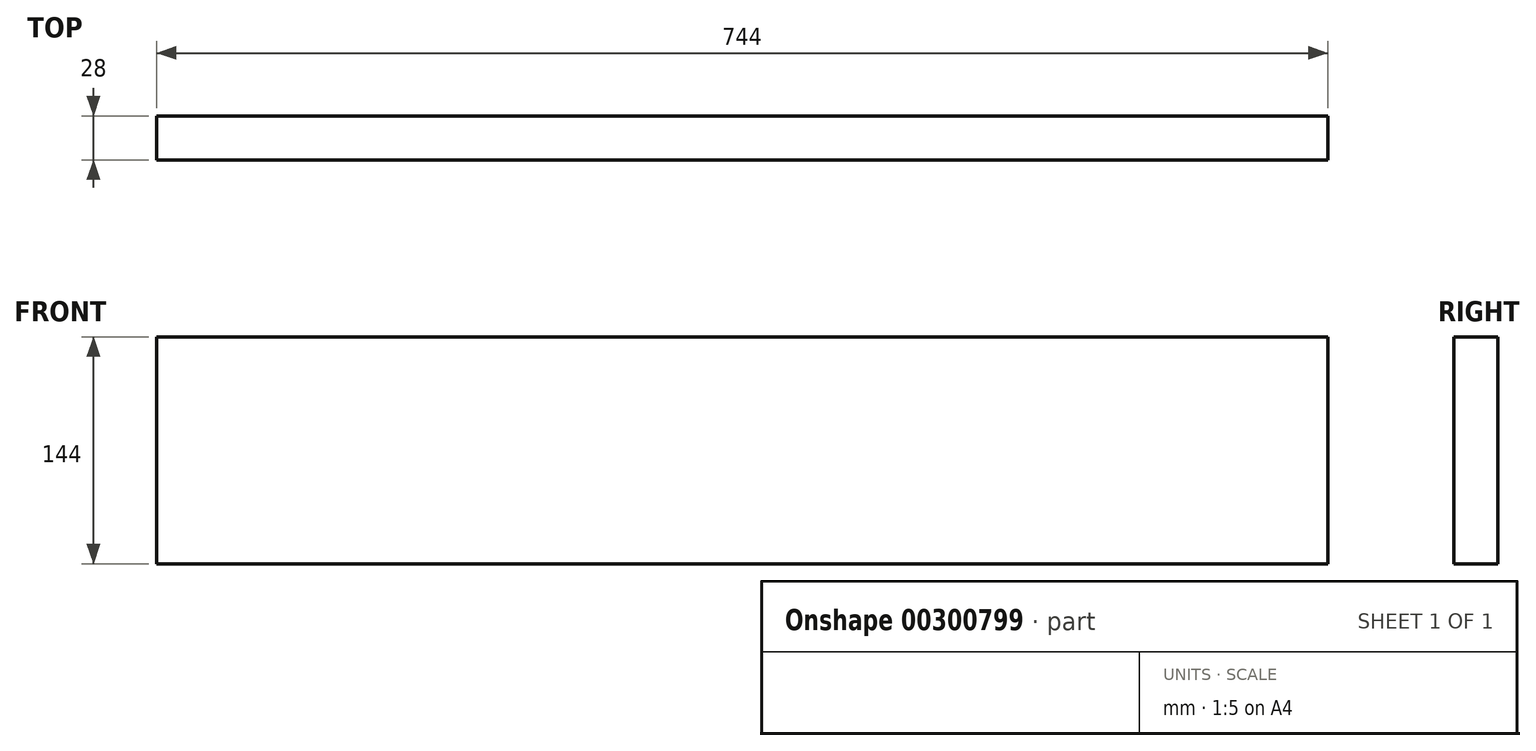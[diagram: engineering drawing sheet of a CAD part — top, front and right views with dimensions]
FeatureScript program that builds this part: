
annotation { "Feature Type Name" : "Feature", "Feature Type Description" : "" }
export const myFeature = defineFeature(function(context is Context, id is Id, definition is map)
    precondition{}
    {
        {
            var Q0;
            Q0=qCreatedBy(makeId("Front.planeOp"),FACE);
            var sketch = newSketch(context, id + "F0", { "sketchPlane" : qUnion([Q0])});
            skLineSegment(sketch, "E0.bottom", {"start": v(-918.71, -213.6) * mm, "end": v(941.29, -213.6) * mm});
            skLineSegment(sketch, "E0.top", {"start": v(-918.71, -573.6) * mm, "end": v(941.29, -573.6) * mm});
            skLineSegment(sketch, "E0.left", {"start": v(-918.71, -213.6) * mm, "end": v(-918.71, -573.6) * mm});
            skLineSegment(sketch, "E0.right", {"start": v(941.29, -213.6) * mm, "end": v(941.29, -573.6) * mm});
            skSolve(sketch);
        }
        {
            var Q0;
            Q0=makeQuery(id+"F0.imprint","IMPRINT",FACE,{"disambiguationData":[TD([[makeQuery(id+"F0.imprint","IMPRINT",EDGE,{"derivedFrom":sQuery(id+"F0.wireOp",EDGE,"E0.bottom")}),-1.0]])]});
            extrude(context, id + "F1", {"entities" : qUnion([Q0]), "depth" : 70 * mm});
        }
        {
            var Q0;
            Q0=makeQuery(id+"F1.opExtrude","SWEPT_BODY",BODY,{"disambiguationData":[OSD([sQuery(id+"F0.wireOp",EDGE,"E0.bottom"),sQuery(id+"F0.wireOp",EDGE,"E0.top"),sQuery(id+"F0.wireOp",EDGE,"E0.left"),sQuery(id+"F0.wireOp",EDGE,"E0.right")])]});
            var Q1;
            Q1=makeQuery(id+"F1.opExtrude","CAP_VERTEX",VERTEX,{"disambiguationData":[OSD([sQuery(id+"F0.wireOp",EDGE,"E0.top"),sQuery(id+"F0.wireOp",EDGE,"E0.right")])],"isStart":false});
            transform(context, id + "F2", {"entities" : qUnion([Q0]), "transformType" : TransformType.SCALE_UNIFORMLY, "scale" : 0.4, "scalePoint" : qUnion([Q1]), "makeCopy" : false});
        }
    });
